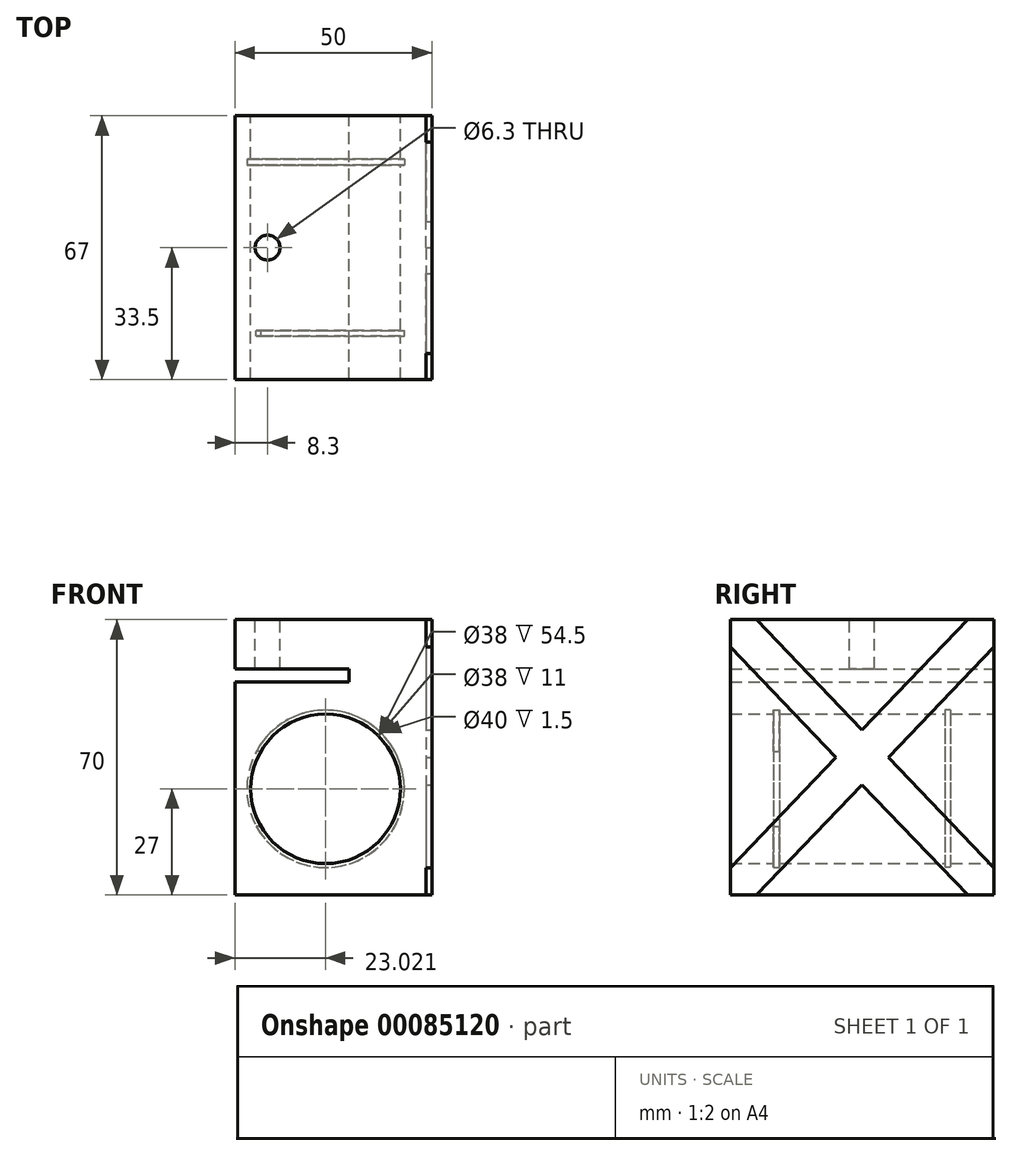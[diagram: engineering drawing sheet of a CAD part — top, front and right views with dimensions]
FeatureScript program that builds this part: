
annotation { "Feature Type Name" : "Feature", "Feature Type Description" : "" }
export const myFeature = defineFeature(function(context is Context, id is Id, definition is map)
    precondition{}
    {
        {
            var Q0;
            Q0=qCreatedBy(makeId("Front.planeOp"),FACE);
            var sketch = newSketch(context, id + "F0", { "sketchPlane" : qUnion([Q0])});
            skLineSegment(sketch, "E0.bottom", {"start": v(0, 0) * mm, "end": v(-50, 0) * mm});
            skLineSegment(sketch, "E0.top", {"start": v(0, 70) * mm, "end": v(-50, 70) * mm});
            skLineSegment(sketch, "E0.left", {"start": v(0, 0) * mm, "end": v(0, 70) * mm});
            skLineSegment(sketch, "E0.right", {"start": v(-50, 0) * mm, "end": v(-50, 70) * mm});
            skSolve(sketch);
        }
        {
            var Q0;
            Q0 = qSketchRegion(id + "F0", true);
            extrude(context, id + "F1", {"entities" : qUnion([Q0]), "depth" : 67 * mm});
        }
        {
            var Q0;
            Q0=makeQuery(id+"F1.opExtrude","SWEPT_FACE",FACE,{"disambiguationData":[OSD([sQuery(id+"F0.wireOp",EDGE,"E0.left")])]});
            var sketch = newSketch(context, id + "F2", { "sketchPlane" : qUnion([Q0])});
            skLineSegment(sketch, "E1.0", {"start": v(-67, 70) * mm, "end": v(0, 70) * mm});
            skLineSegment(sketch, "E1.1", {"start": v(-67, 0) * mm, "end": v(-67, 70) * mm});
            skLineSegment(sketch, "E1.2", {"start": v(0, 0) * mm, "end": v(0, 70) * mm});
            skLineSegment(sketch, "E1.3", {"start": v(-67, 0) * mm, "end": v(0, 0) * mm});
            skLineSegment(sketch, "E2", {"start": v(-67, 70) * mm, "end": v(0, 0) * mm, "construction": true});
            skLineSegment(sketch, "E3", {"start": v(0, 70) * mm, "end": v(-67, 0) * mm, "construction": true});
            skLineSegment(sketch, "E4.0", {"start": v(-70.47, 66.68) * mm, "end": v(-3.47, -3.32) * mm});
            skLineSegment(sketch, "E5.0", {"start": v(-63.53, 73.32) * mm, "end": v(3.47, 3.32) * mm});
            skLineSegment(sketch, "E6.0", {"start": v(-3.47, 73.32) * mm, "end": v(-70.47, 3.32) * mm});
            skLineSegment(sketch, "E7.0", {"start": v(3.47, 66.68) * mm, "end": v(-63.53, -3.32) * mm});
            skSolve(sketch);
        }
        {
            var Q0;
            {var subQ1=sQuery(id+"F2.wireOp",EDGE,"E1.0");var subQ6=sQuery(id+"F2.wireOp",EDGE,"E1.1");var subQ9=makeQuery(id+"F2.imprint","INTERSECT",VERTEX,{"derivedFrom":[subQ1,subQ6]});Q0=makeQuery(id+"F2.imprint","IMPRINT",FACE,{"disambiguationData":[TD([[makeQuery(id+"F2.imprint","IMPRINT",EDGE,{"disambiguationData":[TD([[subQ9,-1.0]])],"derivedFrom":subQ1}),-1.0]])]});}
            var Q1;
            {var subQ1=sQuery(id+"F2.wireOp",EDGE,"E1.0");var subQ7=sQuery(id+"F2.wireOp",EDGE,"E1.2");var subQ8=makeQuery(id+"F2.imprint","INTERSECT",VERTEX,{"derivedFrom":[subQ1,subQ7]});Q1=makeQuery(id+"F2.imprint","IMPRINT",FACE,{"disambiguationData":[TD([[makeQuery(id+"F2.imprint","IMPRINT",EDGE,{"disambiguationData":[TD([[subQ8,1.0]])],"derivedFrom":subQ1}),-1.0]])]});}
            var Q2;
            {var subQ0=sQuery(id+"F2.wireOp",EDGE,"E6.0");var subQ1=sQuery(id+"F2.wireOp",EDGE,"E4.0");var subQ2=makeQuery(id+"F2.imprint","INTERSECT",VERTEX,{"derivedFrom":[subQ1,subQ0]});Q2=makeQuery(id+"F2.imprint","IMPRINT",FACE,{"disambiguationData":[TD([[makeQuery(id+"F2.imprint","IMPRINT",EDGE,{"disambiguationData":[TD([[subQ2,-1.0]])],"derivedFrom":subQ1}),1.0]])]});}
            var Q3;
            {var subQ1=sQuery(id+"F2.wireOp",EDGE,"E1.1");var subQ7=sQuery(id+"F2.wireOp",EDGE,"E1.3");var subQ8=makeQuery(id+"F2.imprint","INTERSECT",VERTEX,{"derivedFrom":[subQ1,subQ7]});Q3=makeQuery(id+"F2.imprint","IMPRINT",FACE,{"disambiguationData":[TD([[makeQuery(id+"F2.imprint","IMPRINT",EDGE,{"disambiguationData":[TD([[subQ8,-1.0]])],"derivedFrom":subQ1}),-1.0]])]});}
            var Q4;
            {var subQ1=sQuery(id+"F2.wireOp",EDGE,"E1.2");var subQ5=sQuery(id+"F2.wireOp",EDGE,"E1.3");var subQ6=makeQuery(id+"F2.imprint","INTERSECT",VERTEX,{"derivedFrom":[subQ1,subQ5]});Q4=makeQuery(id+"F2.imprint","IMPRINT",FACE,{"disambiguationData":[TD([[makeQuery(id+"F2.imprint","IMPRINT",EDGE,{"disambiguationData":[TD([[subQ6,-1.0]])],"derivedFrom":subQ1}),1.0]])]});}
            extrude(context, id + "F3", {"entities" : qUnion([Q0, Q1, Q2, Q3, Q4]), "operationType" : NewBodyOperationType.REMOVE, "oppositeDirection" : true, "depth" : 1.5 * mm});
        }
        {
            var Q0;
            Q0=makeQuery(id+"F1.opExtrude","CAP_FACE",FACE,{"disambiguationData":[OSD([sQuery(id+"F0.wireOp",EDGE,"E0.bottom"),sQuery(id+"F0.wireOp",EDGE,"E0.top"),sQuery(id+"F0.wireOp",EDGE,"E0.left"),sQuery(id+"F0.wireOp",EDGE,"E0.right")])],"isStart":true});
            var sketch = newSketch(context, id + "F4", { "sketchPlane" : qUnion([Q0])});
            skLineSegment(sketch, "E8.0", {"start": v(1.5, 70) * mm, "end": v(50, 70) * mm});
            skLineSegment(sketch, "E8.1", {"start": v(50, 0) * mm, "end": v(50, 70) * mm});
            skLineSegment(sketch, "E9.bottom", {"start": v(50, 57.5) * mm, "end": v(21, 57.5) * mm});
            skLineSegment(sketch, "E9.top", {"start": v(50, 54.2) * mm, "end": v(21, 54.2) * mm});
            skLineSegment(sketch, "E9.left", {"start": v(50, 57.5) * mm, "end": v(50, 54.2) * mm});
            skLineSegment(sketch, "E9.right", {"start": v(21, 57.5) * mm, "end": v(21, 54.2) * mm});
            skCircle(sketch, "E10", {"center": v(26.98, 27) * mm, "radius": 19 * mm});
            skLineSegment(sketch, "E11.bottom", {"start": v(50, 17.5) * mm, "end": v(26.98, 17.5) * mm});
            skLineSegment(sketch, "E11.top", {"start": v(50, 36.5) * mm, "end": v(26.98, 36.5) * mm});
            skLineSegment(sketch, "E11.left", {"start": v(50, 17.5) * mm, "end": v(50, 36.5) * mm});
            skLineSegment(sketch, "E11.right", {"start": v(26.98, 17.5) * mm, "end": v(26.98, 36.5) * mm});
            skLineSegment(sketch, "E12", {"start": v(26.98, 27) * mm, "end": v(87.69, 27) * mm, "construction": true});
            skSolve(sketch);
        }
        {
            var Q0;
            Q0=makeQuery(id+"F4.imprint","IMPRINT",FACE,{"disambiguationData":[TD([[makeQuery(id+"F4.imprint","IMPRINT",EDGE,{"derivedFrom":sQuery(id+"F4.wireOp",EDGE,"E9.bottom")}),1.0]])]});
            var Q1;
            {var subQ5=sQuery(id+"F4.wireOp",EDGE,"E11.right");Q1=makeQuery(id+"F4.imprint","IMPRINT",FACE,{"disambiguationData":[TD([[makeQuery(id+"F4.imprint","IMPRINT",EDGE,{"derivedFrom":subQ5}),1.0]])]});}
            var Q2;
            {var subQ5=sQuery(id+"F4.wireOp",EDGE,"E11.right");Q2=makeQuery(id+"F4.imprint","IMPRINT",FACE,{"disambiguationData":[TD([[makeQuery(id+"F4.imprint","IMPRINT",EDGE,{"derivedFrom":subQ5}),-1.0]])]});}
            var Q3;
            {var subQ5=sQuery(id+"F4.wireOp",EDGE,"E11.left");Q3=makeQuery(id+"F4.imprint","IMPRINT",FACE,{"disambiguationData":[TD([[makeQuery(id+"F4.imprint","IMPRINT",EDGE,{"derivedFrom":subQ5}),1.0]])]});}
            extrude(context, id + "F5", {"entities" : qUnion([Q0, Q1, Q2, Q3]), "operationType" : NewBodyOperationType.REMOVE, "endBound" : BoundingType.THROUGH_ALL, "oppositeDirection" : true, "depth" : 25 * mm});
        }
        {
            var Q0;
            Q0=makeQuery(id+"F1.opExtrude","SWEPT_FACE",FACE,{"disambiguationData":[OSD([sQuery(id+"F0.wireOp",EDGE,"E0.top")])]});
            var sketch = newSketch(context, id + "F6", { "sketchPlane" : qUnion([Q0])});
            skLineSegment(sketch, "E13.0", {"start": v(-1.5, -67) * mm, "end": v(-50, -67) * mm});
            skLineSegment(sketch, "E13.1", {"start": v(-50, -67) * mm, "end": v(-50, 0) * mm});
            skLineSegment(sketch, "E13.2", {"start": v(-1.5, 0) * mm, "end": v(-50, 0) * mm});
            skCircle(sketch, "E14", {"center": v(-41.7, -33.5) * mm, "radius": 3.15 * mm});
            skSolve(sketch);
        }
        {
            var Q0;
            Q0=makeQuery(id+"F6.imprint","IMPRINT",FACE,{"disambiguationData":[TD([[makeQuery(id+"F6.imprint","IMPRINT",EDGE,{"derivedFrom":sQuery(id+"F6.wireOp",EDGE,"E14")}),1.0]])]});
            var Q1;
            Q1=makeQuery(id+"F5.boolean.opBoolean","COPY",FACE,{"derivedFrom":makeQuery(id+"F5.opExtrude","SWEPT_FACE",FACE,{"disambiguationData":[OSD([sQuery(id+"F4.wireOp",EDGE,"E9.bottom")])]})});
            extrude(context, id + "F7", {"entities" : qUnion([Q0]), "operationType" : NewBodyOperationType.REMOVE, "endBound" : BoundingType.UP_TO_SURFACE, "oppositeDirection" : true, "endBoundEntityFace" : qUnion([Q1]), "depth" : 25 * mm});
        }
        {
            var Q0;
            Q0=makeQuery(id+"F1.opExtrude","CAP_FACE",FACE,{"disambiguationData":[OSD([sQuery(id+"F0.wireOp",EDGE,"E0.bottom"),sQuery(id+"F0.wireOp",EDGE,"E0.top"),sQuery(id+"F0.wireOp",EDGE,"E0.left"),sQuery(id+"F0.wireOp",EDGE,"E0.right")])],"isStart":true});
            cPlane(context, id + "F8", {"entities" : qUnion([Q0]), "cplaneType" : CPlaneType.OFFSET, "offset" : 12.5 * mm, "oppositeDirection" : true, "width" : 150 * mm, "height" : 150 * mm});
        }
        {
            var Q0;
            Q0=qCreatedBy(id+"F8.planeOp",FACE);
            var sketch = newSketch(context, id + "F9", { "sketchPlane" : qUnion([Q0])});
            skArc(sketch, "E15.0", {"start": v(43.43, 36.5) * mm, "mid": v(7.98, 27) * mm, "end": v(43.43, 17.5) * mm});
            skCircle(sketch, "E16", {"center": v(26.98, 27) * mm, "radius": 20 * mm});
            skSolve(sketch);
        }
        {
            var Q0;
            Q0=makeQuery(id+"F9.imprint","IMPRINT",FACE,{"disambiguationData":[TD([[makeQuery(id+"F9.imprint","IMPRINT",EDGE,{"derivedFrom":sQuery(id+"F9.wireOp",EDGE,"E16")}),1.0]])]});
            extrude(context, id + "F10", {"entities" : qUnion([Q0]), "operationType" : NewBodyOperationType.REMOVE, "depth" : 1.5 * mm});
        }
        {
            var Q0;
            Q0=makeQuery(id+"F10.boolean.opBoolean","COPY",FACE,{"derivedFrom":makeQuery(id+"F10.opExtrude","CAP_FACE",FACE,{"disambiguationData":[OSD([sQuery(id+"F9.wireOp",EDGE,"E16")])],"isStart":true})});
            cPlane(context, id + "F11", {"entities" : qUnion([Q0]), "cplaneType" : CPlaneType.OFFSET, "offset" : 42 * mm, "oppositeDirection" : true, "width" : 150 * mm, "height" : 150 * mm});
        }
        {
            var Q0;
            Q0=qCreatedBy(id+"F11.planeOp",FACE);
            var sketch = newSketch(context, id + "F12", { "sketchPlane" : qUnion([Q0])});
            skArc(sketch, "E17.0", {"start": v(44.58, 36.5) * mm, "mid": v(6.98, 27) * mm, "end": v(44.58, 17.5) * mm});
            skArc(sketch, "E17.1", {"start": v(43.43, 17.5) * mm, "mid": v(7.98, 27) * mm, "end": v(43.43, 36.5) * mm});
            skLineSegment(sketch, "E17.2", {"start": v(43.43, 36.5) * mm, "end": v(44.58, 36.5) * mm});
            skLineSegment(sketch, "E17.3", {"start": v(43.43, 17.5) * mm, "end": v(44.58, 17.5) * mm});
            skSolve(sketch);
        }
        {
            var Q0;
            Q0 = qSketchRegion(id + "F12", true);
            extrude(context, id + "F13", {"entities" : qUnion([Q0]), "operationType" : NewBodyOperationType.REMOVE, "oppositeDirection" : true, "depth" : 1.5 * mm});
        }
    });
